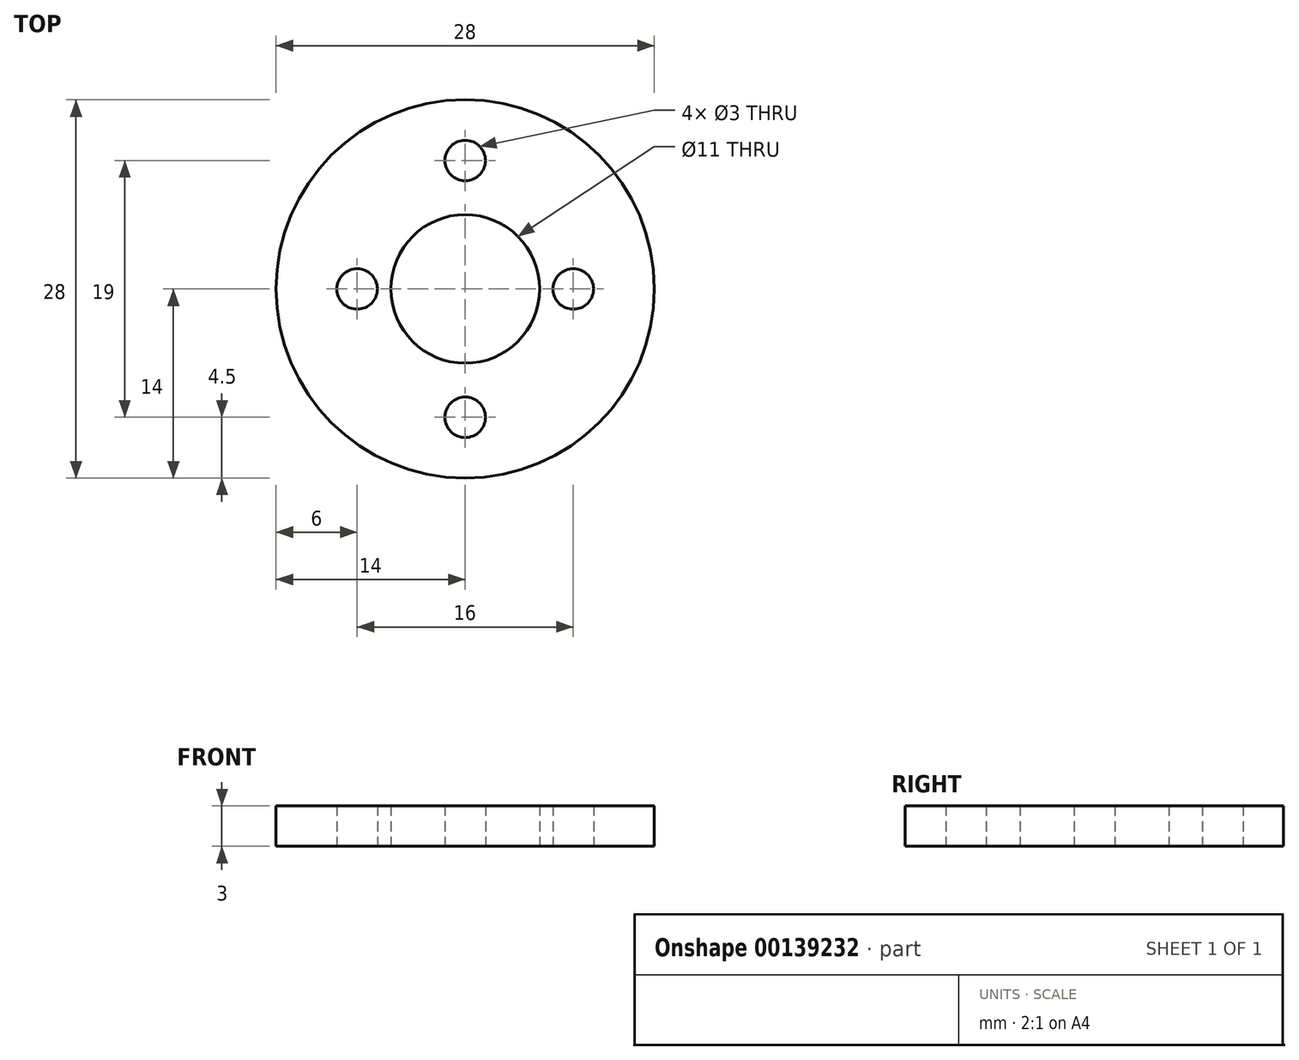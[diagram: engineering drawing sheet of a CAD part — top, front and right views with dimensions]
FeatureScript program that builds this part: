
annotation { "Feature Type Name" : "Feature", "Feature Type Description" : "" }
export const myFeature = defineFeature(function(context is Context, id is Id, definition is map)
    precondition{}
    {
        {
            var Q0;
            Q0=qCreatedBy(makeId("Top.planeOp"),FACE);
            var sketch = newSketch(context, id + "F0", { "sketchPlane" : qUnion([Q0])});
            skCircle(sketch, "E0", {"center": v(0, 0) * mm, "radius": 14 * mm});
            skCircle(sketch, "E1", {"center": v(0, 0) * mm, "radius": 9.5 * mm, "construction": true});
            skLineSegment(sketch, "E2", {"start": v(0, 0) * mm, "end": v(0, 19.1) * mm, "construction": true});
            skLineSegment(sketch, "E3", {"start": v(0, 0) * mm, "end": v(0, -18.78) * mm, "construction": true});
            skCircle(sketch, "E4", {"center": v(0, 9.5) * mm, "radius": 1.5 * mm});
            skCircle(sketch, "E5", {"center": v(0, -9.5) * mm, "radius": 1.5 * mm});
            skCircle(sketch, "E6", {"center": v(0, 0) * mm, "radius": 5.5 * mm});
            skCircle(sketch, "E7", {"center": v(0, 0) * mm, "radius": 8 * mm, "construction": true});
            skLineSegment(sketch, "E8", {"start": v(0, 0) * mm, "end": v(17.12, 0) * mm, "construction": true});
            skLineSegment(sketch, "E9", {"start": v(0, 0) * mm, "end": v(-15.83, 0) * mm, "construction": true});
            skCircle(sketch, "E10", {"center": v(8, 0) * mm, "radius": 1.5 * mm});
            skCircle(sketch, "E11", {"center": v(-8, 0) * mm, "radius": 1.5 * mm});
            skPoint(sketch, "E11.centerSnap0", {"position": v(-7.91, 0) * mm});
            skSolve(sketch);
        }
        {
            var Q0;
            Q0=makeQuery(id+"F0.imprint","IMPRINT",FACE,{"disambiguationData":[TD([[makeQuery(id+"F0.imprint","IMPRINT",EDGE,{"derivedFrom":sQuery(id+"F0.wireOp",EDGE,"E0")}),1.0]])]});
            extrude(context, id + "F1", {"entities" : qUnion([Q0]), "depth" : 3 * mm});
        }
    });
